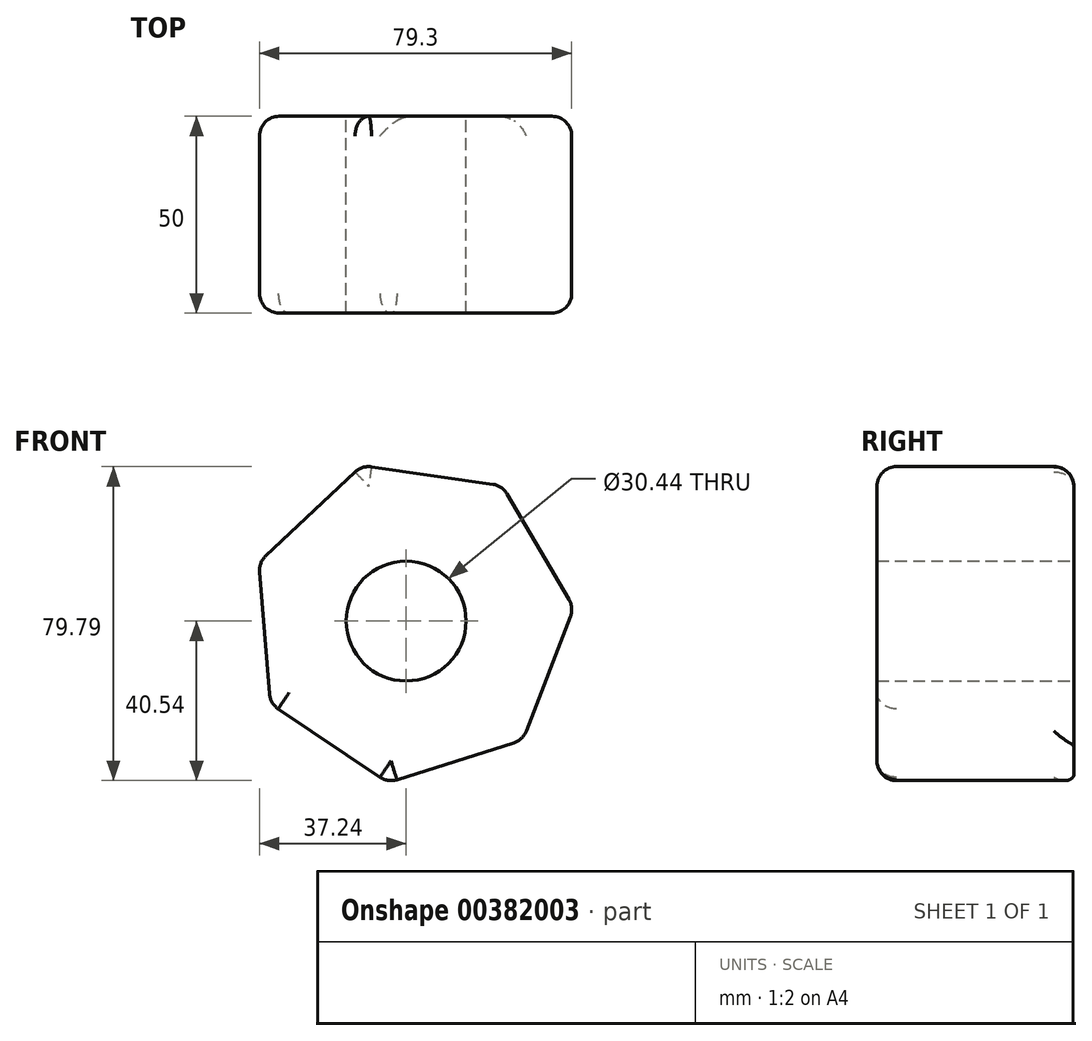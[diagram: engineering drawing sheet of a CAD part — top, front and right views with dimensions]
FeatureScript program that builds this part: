
annotation { "Feature Type Name" : "Feature", "Feature Type Description" : "" }
export const myFeature = defineFeature(function(context is Context, id is Id, definition is map)
    precondition{}
    {
        {
            var Q0;
            Q0=qCreatedBy(makeId("Front.planeOp"),FACE);
            var sketch = newSketch(context, id + "F0", { "sketchPlane" : qUnion([Q0])});
            skCircle(sketch, "E0.cCircle", {"center": v(1.27, 0) * mm, "radius": 37.35 * mm, "construction": true});
            skLineSegment(sketch, "E0.0", {"start": v(-37.42, 14.9) * mm, "end": v(-11.2, 39.54) * mm});
            skLineSegment(sketch, "E0.1", {"start": v(-11.2, 39.54) * mm, "end": v(24.4, 34.4) * mm});
            skLineSegment(sketch, "E0.2", {"start": v(24.4, 34.4) * mm, "end": v(42.6, 3.37) * mm});
            skLineSegment(sketch, "E0.3", {"start": v(42.6, 3.37) * mm, "end": v(29.67, -30.2) * mm});
            skLineSegment(sketch, "E0.4", {"start": v(29.67, -30.2) * mm, "end": v(-4.64, -41.04) * mm});
            skLineSegment(sketch, "E0.5", {"start": v(-4.64, -41.04) * mm, "end": v(-34.5, -20.96) * mm});
            skLineSegment(sketch, "E0.6", {"start": v(-34.5, -20.96) * mm, "end": v(-37.42, 14.9) * mm});
            skPoint(sketch, "E0.0.midPoint", {"position": v(-24.31, 27.22) * mm});
            skSolve(sketch);
        }
        {
            var Q0;
            Q0 = qSketchRegion(id + "F0", true);
            extrude(context, id + "F1", {"entities" : qUnion([Q0]), "depth" : 50 * mm});
        }
        {
            var Q0;
            Q0=qCreatedBy(makeId("Front.planeOp"),FACE);
            var sketch = newSketch(context, id + "F2", { "sketchPlane" : qUnion([Q0])});
            skCircle(sketch, "E1", {"center": v(0, 0) * mm, "radius": 15.22 * mm});
            skSolve(sketch);
        }
        {
            var Q0;
            Q0 = qSketchRegion(id + "F2", true);
            extrude(context, id + "F3", {"entities" : qUnion([Q0]), "operationType" : NewBodyOperationType.REMOVE, "endBound" : BoundingType.THROUGH_ALL, "depth" : 25 * mm});
        }
        {
            var Q0;
            Q0=makeQuery(id+"F1.opExtrude","SWEPT_FACE",FACE,{"disambiguationData":[OSD([sQuery(id+"F0.wireOp",EDGE,"E0.1")])]});
            var Q1;
            Q1=makeQuery(id+"F1.opExtrude","SWEPT_FACE",FACE,{"disambiguationData":[OSD([sQuery(id+"F0.wireOp",EDGE,"E0.2")])]});
            var Q2;
            Q2=makeQuery(id+"F1.opExtrude","SWEPT_FACE",FACE,{"disambiguationData":[OSD([sQuery(id+"F0.wireOp",EDGE,"E0.3")])]});
            var Q3;
            Q3=makeQuery(id+"F1.opExtrude","CAP_EDGE",EDGE,{"disambiguationData":[OSD([sQuery(id+"F0.wireOp",EDGE,"E0.4")])],"isStart":false});
            var Q4;
            Q4=makeQuery(id+"F1.opExtrude","CAP_EDGE",EDGE,{"disambiguationData":[OSD([sQuery(id+"F0.wireOp",EDGE,"E0.5")])],"isStart":false});
            var Q5;
            Q5=makeQuery(id+"F1.opExtrude","CAP_EDGE",EDGE,{"disambiguationData":[OSD([sQuery(id+"F0.wireOp",EDGE,"E0.6")])],"isStart":false});
            var Q6;
            Q6=makeQuery(id+"F1.opExtrude","SWEPT_EDGE",EDGE,{"disambiguationData":[OSD([sQuery(id+"F0.wireOp",EDGE,"E0.0"),sQuery(id+"F0.wireOp",EDGE,"E0.6")])]});
            var Q7;
            Q7=makeQuery(id+"F1.opExtrude","CAP_EDGE",EDGE,{"disambiguationData":[OSD([sQuery(id+"F0.wireOp",EDGE,"E0.0")])],"isStart":false});
            fillet(context, id + "F4", {"entities" : qUnion([Q0, Q1, Q2, Q3, Q4, Q5, Q6, Q7]), "radius" : 5 * mm, "tangentPropagation" : true, "allowEdgeOverflow" : false});
        }
        {
            var Q0;
            Q0=makeQuery(id+"F1.opExtrude","SWEPT_FACE",FACE,{"disambiguationData":[OSD([sQuery(id+"F0.wireOp",EDGE,"E0.6")])]});
            var Q1;
            Q1=makeQuery(id+"F1.opExtrude","SWEPT_FACE",FACE,{"disambiguationData":[OSD([sQuery(id+"F0.wireOp",EDGE,"E0.5")])]});
            fillet(context, id + "F5", {"entities" : qUnion([Q0, Q1]), "radius" : 5 * mm, "tangentPropagation" : true, "allowEdgeOverflow" : false});
        }
    });
